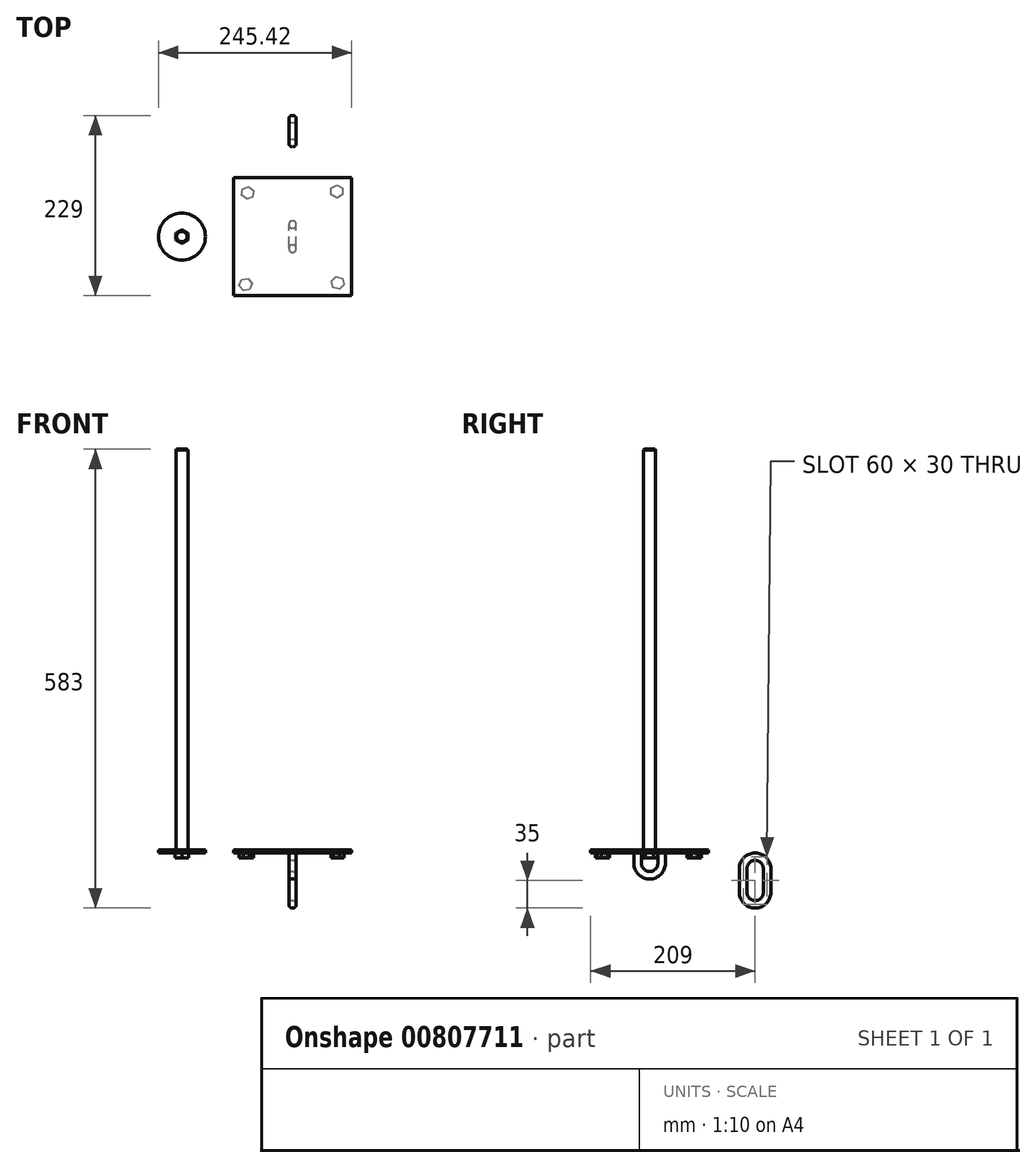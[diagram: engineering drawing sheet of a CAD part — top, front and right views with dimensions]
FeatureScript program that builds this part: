
annotation { "Feature Type Name" : "Feature", "Feature Type Description" : "" }
export const myFeature = defineFeature(function(context is Context, id is Id, definition is map)
    precondition{}
    {
        {
            var Q0;
            Q0=qCreatedBy(makeId("Top.planeOp"),FACE);
            var sketch = newSketch(context, id + "F0", { "sketchPlane" : qUnion([Q0])});
            skLineSegment(sketch, "E0.bottom", {"start": v(-75, 75) * mm, "end": v(75, 75) * mm});
            skLineSegment(sketch, "E0.top", {"start": v(-75, -75) * mm, "end": v(75, -75) * mm});
            skLineSegment(sketch, "E0.left", {"start": v(-75, 75) * mm, "end": v(-75, -75) * mm});
            skLineSegment(sketch, "E0.right", {"start": v(75, 75) * mm, "end": v(75, -75) * mm});
            skCircle(sketch, "E1.cCircle", {"center": v(-56.87, 55.5) * mm, "radius": 7.08 * mm, "construction": true});
            skLineSegment(sketch, "E1.0", {"start": v(-55.69, 63.57) * mm, "end": v(-49.28, 58.5) * mm});
            skLineSegment(sketch, "E1.1", {"start": v(-49.28, 58.5) * mm, "end": v(-50.47, 50.42) * mm});
            skLineSegment(sketch, "E1.2", {"start": v(-50.47, 50.42) * mm, "end": v(-58.06, 47.4) * mm});
            skLineSegment(sketch, "E1.3", {"start": v(-58.06, 47.4) * mm, "end": v(-64.47, 52.48) * mm});
            skLineSegment(sketch, "E1.4", {"start": v(-64.47, 52.48) * mm, "end": v(-63.28, 60.56) * mm});
            skLineSegment(sketch, "E1.5", {"start": v(-63.28, 60.56) * mm, "end": v(-55.69, 63.57) * mm});
            skPoint(sketch, "E1.0.midPoint", {"position": v(-52.48, 61.04) * mm});
            skCircle(sketch, "E2.cCircle", {"center": v(56.23, 57.36) * mm, "radius": 7.08 * mm, "construction": true});
            skLineSegment(sketch, "E2.0", {"start": v(63.3, 61.44) * mm, "end": v(63.3, 53.27) * mm});
            skLineSegment(sketch, "E2.1", {"start": v(63.3, 53.27) * mm, "end": v(56.23, 49.19) * mm});
            skLineSegment(sketch, "E2.2", {"start": v(56.23, 49.19) * mm, "end": v(49.16, 53.27) * mm});
            skLineSegment(sketch, "E2.3", {"start": v(49.16, 53.27) * mm, "end": v(49.16, 61.44) * mm});
            skLineSegment(sketch, "E2.4", {"start": v(49.16, 61.44) * mm, "end": v(56.23, 65.53) * mm});
            skLineSegment(sketch, "E2.5", {"start": v(56.23, 65.53) * mm, "end": v(63.3, 61.44) * mm});
            skPoint(sketch, "E2.0.midPoint", {"position": v(63.3, 57.36) * mm});
            skCircle(sketch, "E3.cCircle", {"center": v(57.41, -58.77) * mm, "radius": 7.08 * mm, "construction": true});
            skLineSegment(sketch, "E3.0", {"start": v(55.39, -50.85) * mm, "end": v(63.25, -53.06) * mm});
            skLineSegment(sketch, "E3.1", {"start": v(63.25, -53.06) * mm, "end": v(65.28, -60.98) * mm});
            skLineSegment(sketch, "E3.2", {"start": v(65.28, -60.98) * mm, "end": v(59.43, -66.69) * mm});
            skLineSegment(sketch, "E3.3", {"start": v(59.43, -66.69) * mm, "end": v(51.57, -64.48) * mm});
            skLineSegment(sketch, "E3.4", {"start": v(51.57, -64.48) * mm, "end": v(49.54, -56.56) * mm});
            skLineSegment(sketch, "E3.5", {"start": v(49.54, -56.56) * mm, "end": v(55.39, -50.85) * mm});
            skPoint(sketch, "E3.0.midPoint", {"position": v(59.32, -51.96) * mm});
            skCircle(sketch, "E4.cCircle", {"center": v(-59.58, -61.09) * mm, "radius": 7.08 * mm, "construction": true});
            skLineSegment(sketch, "E4.0", {"start": v(-56.76, -53.42) * mm, "end": v(-51.53, -59.7) * mm});
            skLineSegment(sketch, "E4.1", {"start": v(-51.53, -59.7) * mm, "end": v(-54.35, -67.36) * mm});
            skLineSegment(sketch, "E4.2", {"start": v(-54.35, -67.36) * mm, "end": v(-62.4, -68.76) * mm});
            skLineSegment(sketch, "E4.3", {"start": v(-62.4, -68.76) * mm, "end": v(-67.63, -62.48) * mm});
            skLineSegment(sketch, "E4.4", {"start": v(-67.63, -62.48) * mm, "end": v(-64.81, -54.81) * mm});
            skLineSegment(sketch, "E4.5", {"start": v(-64.81, -54.81) * mm, "end": v(-56.76, -53.42) * mm});
            skPoint(sketch, "E4.0.midPoint", {"position": v(-54.15, -56.56) * mm});
            skCircle(sketch, "E5.cCircle", {"center": v(-140.54, 0) * mm, "radius": 8.62 * mm, "construction": true});
            skLineSegment(sketch, "E5.0", {"start": v(-131.92, 4.98) * mm, "end": v(-131.92, -4.98) * mm});
            skLineSegment(sketch, "E5.1", {"start": v(-131.92, -4.98) * mm, "end": v(-140.54, -9.95) * mm});
            skLineSegment(sketch, "E5.2", {"start": v(-140.54, -9.95) * mm, "end": v(-149.15, -4.98) * mm});
            skLineSegment(sketch, "E5.3", {"start": v(-149.15, -4.98) * mm, "end": v(-149.15, 4.98) * mm});
            skLineSegment(sketch, "E5.4", {"start": v(-149.15, 4.98) * mm, "end": v(-140.54, 9.95) * mm});
            skLineSegment(sketch, "E5.5", {"start": v(-140.54, 9.95) * mm, "end": v(-131.92, 4.98) * mm});
            skPoint(sketch, "E5.0.midPoint", {"position": v(-131.92, 0) * mm});
            skCircle(sketch, "E6", {"center": v(-140.54, 0) * mm, "radius": 7.59 * mm});
            skCircle(sketch, "E7", {"center": v(-140.54, 0) * mm, "radius": 29.88 * mm});
            skSolve(sketch);
        }
        {
            var Q0;
            Q0=makeQuery(id+"F0.imprint","IMPRINT",FACE,{"disambiguationData":[TD([[makeQuery(id+"F0.imprint","IMPRINT",EDGE,{"derivedFrom":sQuery(id+"F0.wireOp",EDGE,"E3.0")}),-1.0]])]});
            var Q1;
            Q1=makeQuery(id+"F0.imprint","IMPRINT",FACE,{"disambiguationData":[TD([[makeQuery(id+"F0.imprint","IMPRINT",EDGE,{"derivedFrom":sQuery(id+"F0.wireOp",EDGE,"E4.0")}),-1.0]])]});
            var Q2;
            Q2=makeQuery(id+"F0.imprint","IMPRINT",FACE,{"disambiguationData":[TD([[makeQuery(id+"F0.imprint","IMPRINT",EDGE,{"derivedFrom":sQuery(id+"F0.wireOp",EDGE,"E1.0")}),-1.0]])]});
            var Q3;
            Q3=makeQuery(id+"F0.imprint","IMPRINT",FACE,{"disambiguationData":[TD([[makeQuery(id+"F0.imprint","IMPRINT",EDGE,{"derivedFrom":sQuery(id+"F0.wireOp",EDGE,"E2.0")}),-1.0]])]});
            var Q4;
            Q4=makeQuery(id+"F0.imprint","IMPRINT",FACE,{"disambiguationData":[TD([[makeQuery(id+"F0.imprint","IMPRINT",EDGE,{"derivedFrom":sQuery(id+"F0.wireOp",EDGE,"E0.bottom")}),-1.0]])]});
            var Q5;
            Q5=makeQuery(id+"F0.imprint","IMPRINT",FACE,{"disambiguationData":[TD([[makeQuery(id+"F0.imprint","IMPRINT",EDGE,{"derivedFrom":sQuery(id+"F0.wireOp",EDGE,"E5.0")}),-1.0]])]});
            var Q6;
            Q6=makeQuery(id+"F0.imprint","IMPRINT",FACE,{"disambiguationData":[TD([[makeQuery(id+"F0.imprint","IMPRINT",EDGE,{"derivedFrom":sQuery(id+"F0.wireOp",EDGE,"E5.0")}),1.0]])]});
            extrude(context, id + "F1", {"entities" : qUnion([Q0, Q1, Q2, Q3, Q4, Q5, Q6]), "depth" : 4 * mm, "offsetDistance" : 25 * mm});
        }
        {
            var Q0;
            Q0=makeQuery(id+"F0.imprint","IMPRINT",FACE,{"disambiguationData":[TD([[makeQuery(id+"F0.imprint","IMPRINT",EDGE,{"derivedFrom":sQuery(id+"F0.wireOp",EDGE,"E1.0")}),-1.0]])]});
            var Q1;
            Q1=makeQuery(id+"F0.imprint","IMPRINT",FACE,{"disambiguationData":[TD([[makeQuery(id+"F0.imprint","IMPRINT",EDGE,{"derivedFrom":sQuery(id+"F0.wireOp",EDGE,"E2.0")}),-1.0]])]});
            var Q2;
            Q2=makeQuery(id+"F0.imprint","IMPRINT",FACE,{"disambiguationData":[TD([[makeQuery(id+"F0.imprint","IMPRINT",EDGE,{"derivedFrom":sQuery(id+"F0.wireOp",EDGE,"E3.0")}),-1.0]])]});
            var Q3;
            Q3=makeQuery(id+"F0.imprint","IMPRINT",FACE,{"disambiguationData":[TD([[makeQuery(id+"F0.imprint","IMPRINT",EDGE,{"derivedFrom":sQuery(id+"F0.wireOp",EDGE,"E4.0")}),-1.0]])]});
            var Q4;
            Q4=makeQuery(id+"F0.imprint","IMPRINT",FACE,{"disambiguationData":[TD([[makeQuery(id+"F0.imprint","IMPRINT",EDGE,{"derivedFrom":sQuery(id+"F0.wireOp",EDGE,"E6")}),1.0]])]});
            var Q5;
            Q5=makeQuery(id+"F0.imprint","IMPRINT",FACE,{"disambiguationData":[TD([[makeQuery(id+"F0.imprint","IMPRINT",EDGE,{"derivedFrom":sQuery(id+"F0.wireOp",EDGE,"E5.0")}),-1.0]])]});
            extrude(context, id + "F2", {"entities" : qUnion([Q0, Q1, Q2, Q3, Q4, Q5]), "operationType" : NewBodyOperationType.ADD, "oppositeDirection" : true, "depth" : 6 * mm, "offsetDistance" : 25 * mm});
        }
        {
            var Q0;
            Q0=qCreatedBy(makeId("Right.planeOp"),FACE);
            var sketch = newSketch(context, id + "F3", { "sketchPlane" : qUnion([Q0])});
            skLineSegment(sketch, "E8.left", {"start": v(114, -20) * mm, "end": v(114, -50) * mm});
            skLineSegment(sketch, "E8.right", {"start": v(154, -20) * mm, "end": v(154, -50) * mm});
            skPoint(sketch, "E9", {"position": v(114, -20) * mm});
            skArc(sketch, "E10", {"start": v(154, -20) * mm, "mid": v(134, 0) * mm, "end": v(114, -20) * mm});
            skPoint(sketch, "E11", {"position": v(114, -50) * mm});
            skArc(sketch, "E12", {"start": v(114, -50) * mm, "mid": v(134, -70) * mm, "end": v(154, -50) * mm});
            skPoint(sketch, "E13.orphan", {"position": v(134, 0) * mm});
            skPoint(sketch, "E14.end.orphan", {"position": v(134, -70) * mm});
            skArc(sketch, "E15.0", {"start": v(144.5, -20) * mm, "mid": v(134, -9.5) * mm, "end": v(123.5, -20) * mm});
            skLineSegment(sketch, "E15.1", {"start": v(144.5, -20) * mm, "end": v(144.5, -50) * mm});
            skArc(sketch, "E15.2", {"start": v(123.5, -50) * mm, "mid": v(134, -60.5) * mm, "end": v(144.5, -50) * mm});
            skLineSegment(sketch, "E15.3", {"start": v(123.5, -20) * mm, "end": v(123.5, -50) * mm});
            skLineSegment(sketch, "E16.left", {"start": v(-20, 0) * mm, "end": v(-20, -13.11) * mm});
            skLineSegment(sketch, "E16.right", {"start": v(20, 0) * mm, "end": v(20, -13.11) * mm});
            skPoint(sketch, "E17", {"position": v(-20, -13.11) * mm});
            skArc(sketch, "E18", {"start": v(-20, -13.11) * mm, "mid": v(0, -33.11) * mm, "end": v(20, -13.11) * mm});
            skPoint(sketch, "E19.end.orphan", {"position": v(0, -33.11) * mm});
            skLineSegment(sketch, "E20.1", {"start": v(10.5, 0) * mm, "end": v(10.5, -13.11) * mm});
            skArc(sketch, "E20.2", {"start": v(-10.5, -13.11) * mm, "mid": v(0, -23.61) * mm, "end": v(10.5, -13.11) * mm});
            skLineSegment(sketch, "E20.3", {"start": v(-10.5, 0) * mm, "end": v(-10.5, -13.11) * mm});
            skLineSegment(sketch, "E21", {"start": v(-20, 0) * mm, "end": v(20, 0) * mm});
            skSolve(sketch);
        }
        {
            var Q0;
            Q0=makeQuery(id+"F3.imprint","IMPRINT",FACE,{"disambiguationData":[TD([[makeQuery(id+"F3.imprint","IMPRINT",EDGE,{"derivedFrom":sQuery(id+"F3.wireOp",EDGE,"E8.left")}),1.0]])]});
            var Q1;
            {var subQ2=sQuery(id+"F3.wireOp",EDGE,"E16.left");Q1=makeQuery(id+"F3.imprint","IMPRINT",FACE,{"disambiguationData":[TD([[makeQuery(id+"F3.imprint","IMPRINT",EDGE,{"derivedFrom":subQ2}),1.0]])]});}
            extrude(context, id + "F4", {"entities" : qUnion([Q0, Q1]), "operationType" : NewBodyOperationType.ADD, "depth" : 9.5 * mm, "offsetDistance" : 25 * mm, "symmetric" : true});
        }
        {
            var Q0;
            Q0=makeQuery(id+"F4.opExtrude","CAP_FACE",FACE,{"disambiguationData":[OSD([sQuery(id+"F3.wireOp",EDGE,"E8.left"),sQuery(id+"F3.wireOp",EDGE,"E8.right"),sQuery(id+"F3.wireOp",EDGE,"E10"),sQuery(id+"F3.wireOp",EDGE,"E12"),sQuery(id+"F3.wireOp",EDGE,"E15.0"),sQuery(id+"F3.wireOp",EDGE,"E15.1"),sQuery(id+"F3.wireOp",EDGE,"E15.2"),sQuery(id+"F3.wireOp",EDGE,"E15.3")])],"isStart":false});
            var Q1;
            Q1=makeQuery(id+"F4.opExtrude","CAP_FACE",FACE,{"disambiguationData":[OSD([sQuery(id+"F3.wireOp",EDGE,"E8.left"),sQuery(id+"F3.wireOp",EDGE,"E8.right"),sQuery(id+"F3.wireOp",EDGE,"E10"),sQuery(id+"F3.wireOp",EDGE,"E12"),sQuery(id+"F3.wireOp",EDGE,"E15.0"),sQuery(id+"F3.wireOp",EDGE,"E15.1"),sQuery(id+"F3.wireOp",EDGE,"E15.2"),sQuery(id+"F3.wireOp",EDGE,"E15.3")])],"isStart":true});
            var Q2;
            Q2=makeQuery(id+"F4.opExtrude","CAP_EDGE",EDGE,{"disambiguationData":[OSD([sQuery(id+"F3.wireOp",EDGE,"E20.1")])],"isStart":false});
            var Q3;
            Q3=makeQuery(id+"F4.opExtrude","CAP_EDGE",EDGE,{"disambiguationData":[OSD([sQuery(id+"F3.wireOp",EDGE,"E20.2")])],"isStart":false});
            var Q4;
            Q4=makeQuery(id+"F4.opExtrude","CAP_EDGE",EDGE,{"disambiguationData":[OSD([sQuery(id+"F3.wireOp",EDGE,"E20.2")])],"isStart":true});
            var Q5;
            Q5=makeQuery(id+"F4.opExtrude","CAP_EDGE",EDGE,{"disambiguationData":[OSD([sQuery(id+"F3.wireOp",EDGE,"E18")])],"isStart":true});
            var Q6;
            Q6=makeQuery(id+"F4.opExtrude","CAP_EDGE",EDGE,{"disambiguationData":[OSD([sQuery(id+"F3.wireOp",EDGE,"E18")])],"isStart":false});
            fillet(context, id + "F5", {"entities" : qUnion([Q0, Q1, Q2, Q3, Q4, Q5, Q6]), "radius" : 4.5 * mm, "tangentPropagation" : true, "allowEdgeOverflow" : false});
        }
        {
            var Q0;
            Q0=makeQuery(id+"F0.imprint","IMPRINT",FACE,{"disambiguationData":[TD([[makeQuery(id+"F0.imprint","IMPRINT",EDGE,{"derivedFrom":sQuery(id+"F0.wireOp",EDGE,"E6")}),1.0]])]});
            extrude(context, id + "F6", {"entities" : qUnion([Q0]), "operationType" : NewBodyOperationType.ADD, "depth" : 513 * mm, "offsetDistance" : 25 * mm});
        }
        {
            var Q0;
            Q0=makeQuery(id+"F6.opExtrude","CAP_EDGE",EDGE,{"disambiguationData":[OSD([sQuery(id+"F0.wireOp",EDGE,"E6")])],"isStart":false});
            chamfer(context, id + "F7", {"entities" : qUnion([Q0]), "width" : 1 * mm, "tangentPropagation" : true});
        }
    });
